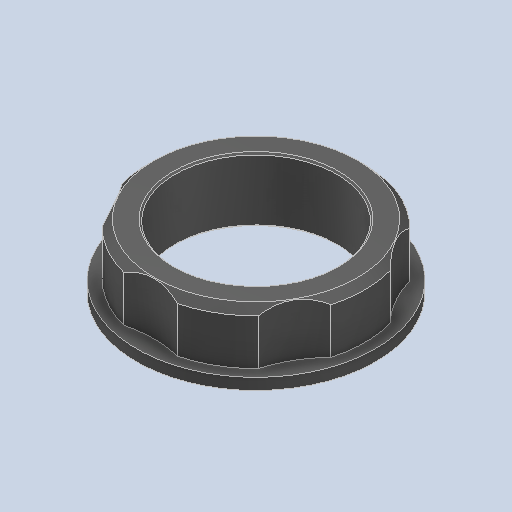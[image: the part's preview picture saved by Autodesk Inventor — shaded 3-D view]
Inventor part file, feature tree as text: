
AUTODESK INVENTOR PART (.ipt)
format: ipt  version: 2022 (Build 260153000, 153)  size: 147,456 bytes
history: native  units: in
note: dims shown in document units (in); Inventor stores cm internally (conversion verified against a paired STEP export)
features: chamfer x1
ambient origin geometry x8: Origin, YZ Plane, XZ Plane, XY Plane, X Axis, Y Axis, Z Axis, Center Point
bodies: Solid1 (feature_tree)
feature tree (1):
  chamfer  "Fase2"  [1 undecoded]
note: 1 required parameter value undecoded (feature->parameter linkage not recoverable at this tier; creation-order binding heuristic only, values carry confidence <= 0.55)
